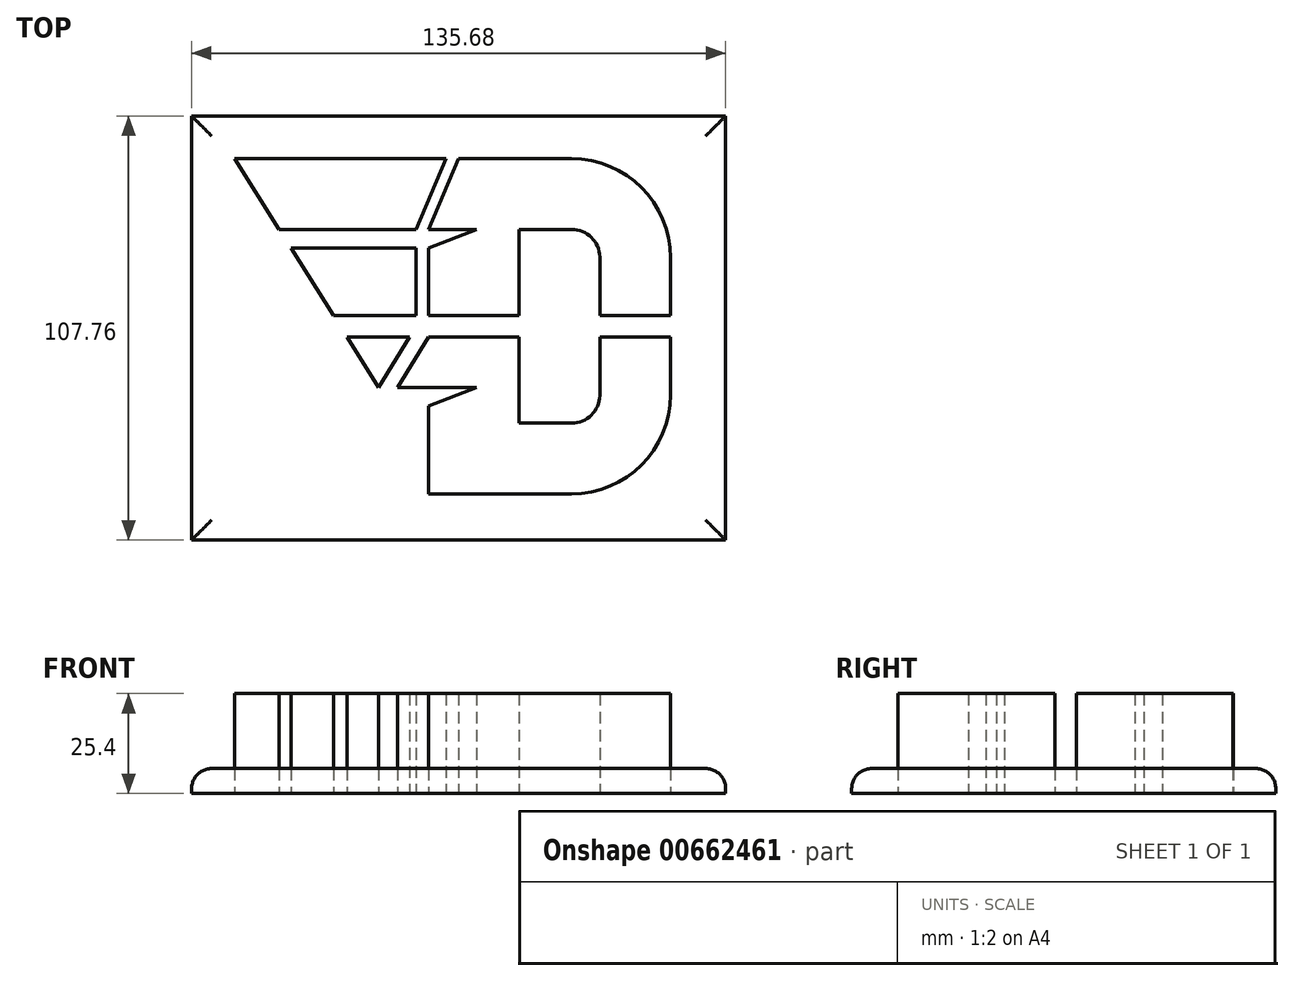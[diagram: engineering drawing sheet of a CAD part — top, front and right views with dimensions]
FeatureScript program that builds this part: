
annotation { "Feature Type Name" : "Feature", "Feature Type Description" : "" }
export const myFeature = defineFeature(function(context is Context, id is Id, definition is map)
    precondition{}
    {
        {
            var Q0;
            Q0=qCreatedBy(makeId("Top.planeOp"),FACE);
            var sketch = newSketch(context, id + "F0", { "sketchPlane" : qUnion([Q0])});
            skLineSegment(sketch, "E0", {"start": v(-15.38, 24.63) * mm, "end": v(-7.68, 42.64) * mm});
            skLineSegment(sketch, "E1", {"start": v(-7.68, 42.64) * mm, "end": v(-61.49, 42.64) * mm});
            skLineSegment(sketch, "E2", {"start": v(-61.49, 42.64) * mm, "end": v(-50.14, 24.63) * mm});
            skLineSegment(sketch, "E3", {"start": v(-24.83, -15.55) * mm, "end": v(-17.04, -2.74) * mm});
            skLineSegment(sketch, "E4", {"start": v(-36.35, 2.74) * mm, "end": v(-15.38, 2.74) * mm});
            skLineSegment(sketch, "E5", {"start": v(-15.38, 2.74) * mm, "end": v(-15.38, 19.9) * mm});
            skLineSegment(sketch, "E6", {"start": v(-15.38, 19.9) * mm, "end": v(-47.17, 19.9) * mm});
            skLineSegment(sketch, "E7", {"start": v(-47.17, 19.9) * mm, "end": v(-36.35, 2.74) * mm});
            skLineSegment(sketch, "E8", {"start": v(-15.38, 24.63) * mm, "end": v(-50.14, 24.63) * mm});
            skLineSegment(sketch, "E9.trimOffspring", {"start": v(-32.9, -2.74) * mm, "end": v(-24.83, -15.55) * mm});
            skPoint(sketch, "E10.end.orphan", {"position": v(56.46, 6.9) * mm});
            skPoint(sketch, "E11.end.orphan", {"position": v(56.46, 0) * mm});
            skPoint(sketch, "E11.start.orphan", {"position": v(-4.52, 0) * mm});
            skPoint(sketch, "E12.end.orphan", {"position": v(-4.55, 34.73) * mm});
            skPoint(sketch, "E12.start.orphan", {"position": v(-4.55, 42.57) * mm});
            skLineSegment(sketch, "E13", {"start": v(-4.55, 42.57) * mm, "end": v(-12.22, 24.63) * mm});
            skLineSegment(sketch, "E14", {"start": v(-12.22, 24.63) * mm, "end": v(0, 24.63) * mm});
            skLineSegment(sketch, "E15", {"start": v(0, 24.63) * mm, "end": v(-12.22, 19.9) * mm});
            skLineSegment(sketch, "E16", {"start": v(-12.22, 19.9) * mm, "end": v(-12.22, 2.74) * mm});
            skLineSegment(sketch, "E17", {"start": v(-12.22, 2.74) * mm, "end": v(10.85, 2.74) * mm});
            skLineSegment(sketch, "E18", {"start": v(10.85, 2.74) * mm, "end": v(10.85, 24.63) * mm});
            skLineSegment(sketch, "E19", {"start": v(10.85, 24.63) * mm, "end": v(24.18, 24.63) * mm});
            skArc(sketch, "E20", {"start": v(24.18, 24.63) * mm, "mid": v(29.2, 22.57) * mm, "end": v(31.32, 17.6) * mm});
            skLineSegment(sketch, "E21", {"start": v(31.32, 17.6) * mm, "end": v(31.32, 2.74) * mm});
            skLineSegment(sketch, "E22", {"start": v(31.32, 2.74) * mm, "end": v(49.27, 2.74) * mm});
            skArc(sketch, "E23", {"start": v(24.18, 42.57) * mm, "mid": v(41.92, 35.22) * mm, "end": v(49.27, 17.48) * mm});
            skLineSegment(sketch, "E24", {"start": v(49.27, 17.48) * mm, "end": v(49.27, 2.74) * mm});
            skLineSegment(sketch, "E25", {"start": v(24.18, 42.57) * mm, "end": v(-4.55, 42.57) * mm});
            skLineSegment(sketch, "E26.MirrorCS", {"start": v(-12.22, -2.74) * mm, "end": v(10.85, -2.74) * mm});
            skLineSegment(sketch, "E27.MirrorCS", {"start": v(10.85, -2.74) * mm, "end": v(10.85, -24.63) * mm});
            skLineSegment(sketch, "E28.MirrorCS", {"start": v(31.32, -17.6) * mm, "end": v(31.32, -2.74) * mm});
            skArc(sketch, "E29.MirrorCS", {"start": v(24.18, -24.63) * mm, "mid": v(29.2, -22.57) * mm, "end": v(31.32, -17.6) * mm});
            skLineSegment(sketch, "E30.MirrorCS", {"start": v(10.85, -24.63) * mm, "end": v(24.18, -24.63) * mm});
            skLineSegment(sketch, "E31.MirrorCS", {"start": v(31.32, -2.74) * mm, "end": v(49.27, -2.74) * mm});
            skLineSegment(sketch, "E32.MirrorCS", {"start": v(49.27, -17.48) * mm, "end": v(49.27, -2.74) * mm});
            skArc(sketch, "E33.MirrorCS", {"start": v(24.18, -42.57) * mm, "mid": v(41.92, -35.22) * mm, "end": v(49.27, -17.48) * mm});
            skLineSegment(sketch, "E34.MirrorCS", {"start": v(24.18, -42.57) * mm, "end": v(-4.55, -42.57) * mm});
            skLineSegment(sketch, "E35", {"start": v(-12.22, -2.74) * mm, "end": v(-20.01, -15.55) * mm});
            skLineSegment(sketch, "E36", {"start": v(-20.01, -15.55) * mm, "end": v(0, -15.55) * mm});
            skLineSegment(sketch, "E37", {"start": v(0, -15.55) * mm, "end": v(-12.22, -20.26) * mm});
            skLineSegment(sketch, "E38", {"start": v(-12.22, -20.26) * mm, "end": v(-12.22, -42.57) * mm});
            skLineSegment(sketch, "E39", {"start": v(-12.22, -42.57) * mm, "end": v(-4.55, -42.57) * mm});
            skLineSegment(sketch, "E40", {"start": v(-17.04, -2.74) * mm, "end": v(-32.9, -2.74) * mm});
            skPoint(sketch, "E41.end.orphan", {"position": v(-34.63, 0) * mm});
            skPoint(sketch, "E42.orphan", {"position": v(-15.38, 0) * mm});
            skSolve(sketch);
        }
        {
            var Q0;
            Q0=makeQuery(id+"F0.imprint","IMPRINT",FACE,{"disambiguationData":[TD([[makeQuery(id+"F0.imprint","IMPRINT",EDGE,{"derivedFrom":sQuery(id+"F0.wireOp",EDGE,"E4")}),1.0]])]});
            var Q1;
            Q1=makeQuery(id+"F0.imprint","IMPRINT",FACE,{"disambiguationData":[TD([[makeQuery(id+"F0.imprint","IMPRINT",EDGE,{"derivedFrom":sQuery(id+"F0.wireOp",EDGE,"E13")}),1.0]])]});
            var Q2;
            Q2=makeQuery(id+"F0.imprint","IMPRINT",FACE,{"disambiguationData":[TD([[makeQuery(id+"F0.imprint","IMPRINT",EDGE,{"derivedFrom":sQuery(id+"F0.wireOp",EDGE,"E26.MirrorCS")}),-1.0]])]});
            var Q3;
            Q3=makeQuery(id+"F0.imprint","IMPRINT",FACE,{"disambiguationData":[TD([[makeQuery(id+"F0.imprint","IMPRINT",EDGE,{"derivedFrom":sQuery(id+"F0.wireOp",EDGE,"E0")}),1.0]])]});
            var Q4;
            Q4=makeQuery(id+"F0.imprint","IMPRINT",FACE,{"disambiguationData":[TD([[makeQuery(id+"F0.imprint","IMPRINT",EDGE,{"derivedFrom":sQuery(id+"F0.wireOp",EDGE,"E3")}),1.0]])]});
            extrude(context, id + "F1", {"entities" : qUnion([Q0, Q1, Q2, Q3, Q4]), "depth" : 25.4 * mm, "offsetDistance" : 25.4 * mm});
        }
        {
            var Q0;
            Q0=qCreatedBy(makeId("Top.planeOp"),FACE);
            var sketch = newSketch(context, id + "F2", { "sketchPlane" : qUnion([Q0])});
            skLineSegment(sketch, "E43.bottom", {"start": v(-72.37, 53.43) * mm, "end": v(63.3, 53.43) * mm});
            skLineSegment(sketch, "E43.top", {"start": v(-72.37, -54.33) * mm, "end": v(63.3, -54.33) * mm});
            skLineSegment(sketch, "E43.left", {"start": v(-72.37, 53.43) * mm, "end": v(-72.37, -54.33) * mm});
            skLineSegment(sketch, "E43.right", {"start": v(63.3, 53.43) * mm, "end": v(63.3, -54.33) * mm});
            skSolve(sketch);
        }
        {
            var Q0;
            Q0 = qSketchRegion(id + "F2", true);
            extrude(context, id + "F3", {"entities" : qUnion([Q0]), "depth" : 6.35 * mm, "offsetDistance" : 25.4 * mm});
        }
        {
            var Q0;
            Q0=makeQuery(id+"F3.opExtrude","CAP_EDGE",EDGE,{"disambiguationData":[OSD([sQuery(id+"F2.wireOp",EDGE,"E43.bottom")])],"isStart":false});
            var Q1;
            Q1=makeQuery(id+"F3.opExtrude","CAP_EDGE",EDGE,{"disambiguationData":[OSD([sQuery(id+"F2.wireOp",EDGE,"E43.left")])],"isStart":false});
            var Q2;
            Q2=makeQuery(id+"F3.opExtrude","CAP_EDGE",EDGE,{"disambiguationData":[OSD([sQuery(id+"F2.wireOp",EDGE,"E43.right")])],"isStart":false});
            var Q3;
            Q3=makeQuery(id+"F3.opExtrude","CAP_EDGE",EDGE,{"disambiguationData":[OSD([sQuery(id+"F2.wireOp",EDGE,"E43.top")])],"isStart":false});
            fillet(context, id + "F4", {"entities" : qUnion([Q0, Q1, Q2, Q3]), "radius" : 5.08 * mm, "tangentPropagation" : true, "allowEdgeOverflow" : false});
        }
    });
